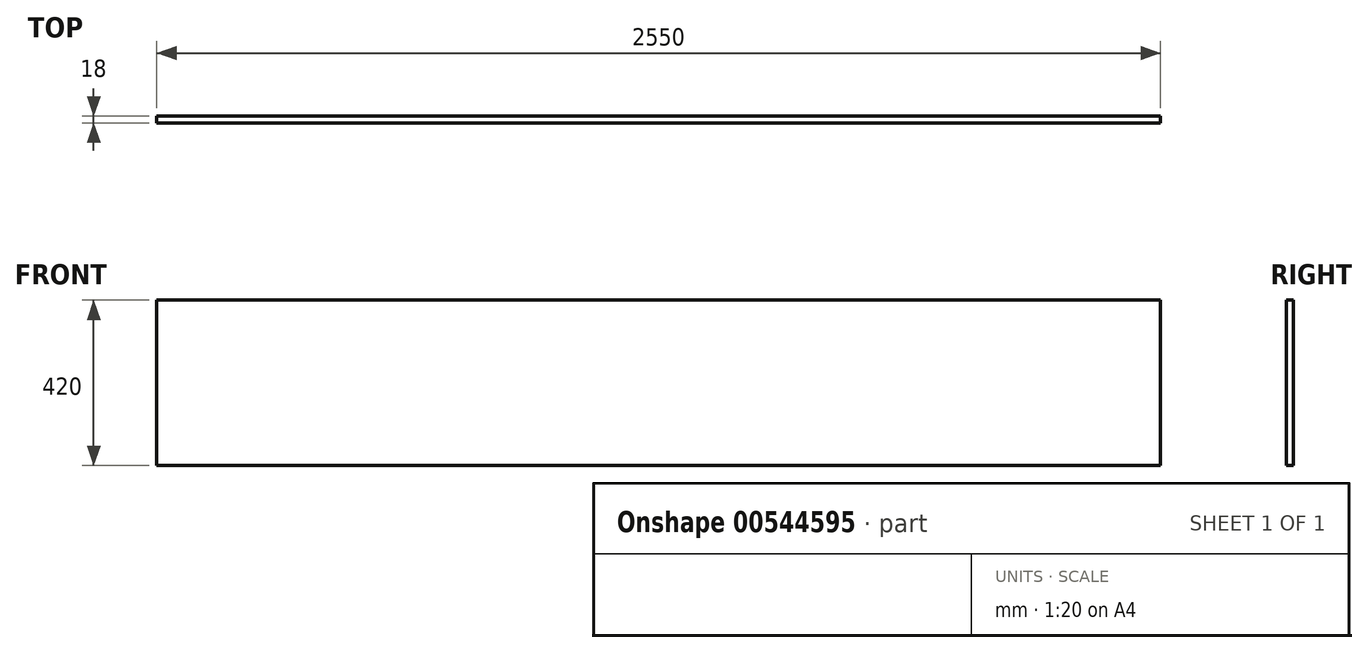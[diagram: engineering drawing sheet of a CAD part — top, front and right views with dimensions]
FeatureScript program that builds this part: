
annotation { "Feature Type Name" : "Feature", "Feature Type Description" : "" }
export const myFeature = defineFeature(function(context is Context, id is Id, definition is map)
    precondition{}
    {
        {
            var Q0;
            Q0=qCreatedBy(makeId("Front.planeOp"),FACE);
            var sketch = newSketch(context, id + "F0", { "sketchPlane" : qUnion([Q0])});
            skLineSegment(sketch, "E0.bottom", {"start": v(-1282.86, -717.04) * mm, "end": v(1267.14, -717.04) * mm});
            skLineSegment(sketch, "E0.top", {"start": v(-1282.86, -297.04) * mm, "end": v(1267.14, -297.04) * mm});
            skLineSegment(sketch, "E0.left", {"start": v(-1282.86, -717.04) * mm, "end": v(-1282.86, -297.04) * mm});
            skLineSegment(sketch, "E0.right", {"start": v(1267.14, -717.04) * mm, "end": v(1267.14, -297.04) * mm});
            skSolve(sketch);
        }
        {
            var Q0;
            Q0 = qSketchRegion(id + "F0", true);
            extrude(context, id + "F1", {"entities" : qUnion([Q0]), "oppositeDirection" : true, "depth" : 18 * mm, "offsetDistance" : 25 * mm});
        }
    });
